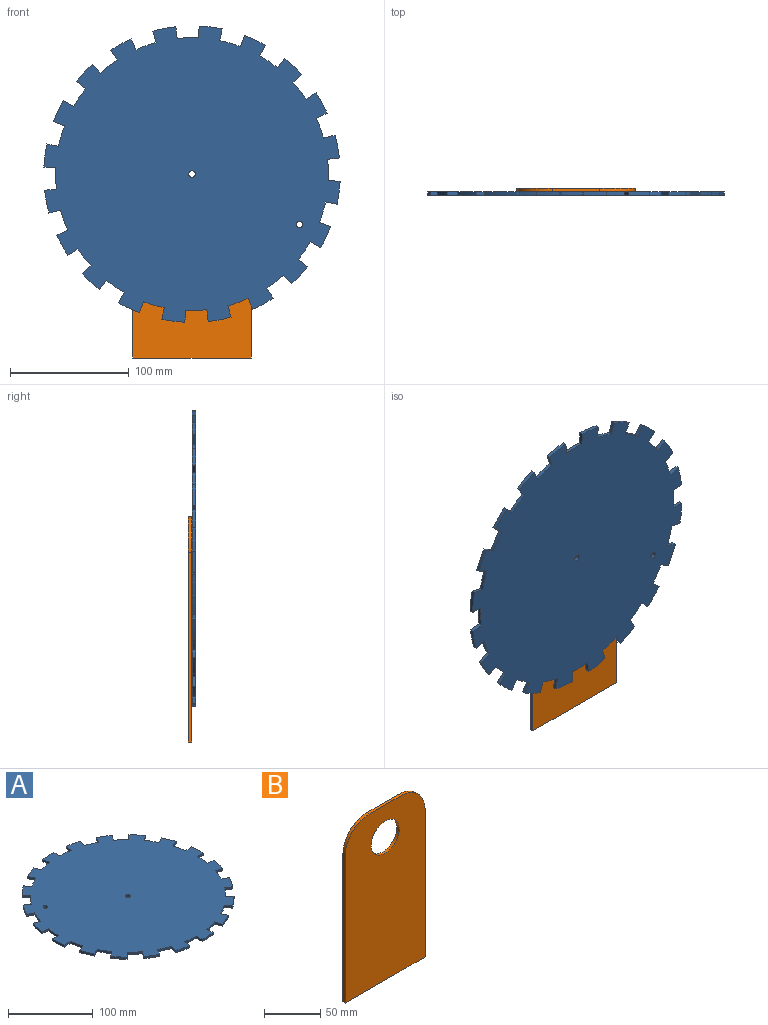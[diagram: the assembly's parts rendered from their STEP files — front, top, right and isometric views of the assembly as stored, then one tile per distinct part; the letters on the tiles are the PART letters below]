
ASSEMBLY  parts=2 mates=1
PART A: 84 faces, bbox 250x250x3 mm
  f0: plane 250x250mm, normal (0,0,1), area 45270mm2, adj f2,f3,f4,f5,f6,f7,f8,f9
  f1: plane 250x250mm, normal (0,0,-1), area 45270mm2, adj f2,f3,f4,f5,f6,f7,f8,f9
  f2: cylinder r=115mm len=17.98mm, axis (0,0,-1), area 54.2mm2, adj f0,f1,f3,f81
  f3: plane 10x3mm, normal (1,-0.01,0), area 30mm2, adj f0,f1,f2,f4
  f4: cylinder r=125mm len=19.57mm, axis (0,0,-1), area 58.9mm2, adj f0,f1,f3,f5
  f5: plane 9.89x3mm, normal (-0.99,-0.15,0), area 30mm2, adj f0,f1,f4,f6
  f6: cylinder r=115mm len=17.58mm, axis (0,0,-1), area 54.2mm2, adj f0,f1,f5,f7
  f7: plane 9.54x3.01mm, normal (0.95,0.3,0), area 30mm2, adj f0,f1,f6,f8
  f8: cylinder r=125mm len=18.18mm, axis (0,0,-1), area 58.9mm2, adj f0,f1,f7,f9
  f9: plane 8.95x4.46mm, normal (-0.89,-0.45,0), area 30mm2, adj f0,f1,f8,f10
  f10: cylinder r=115mm len=15.47mm, axis (0,0,-1), area 54.2mm2, adj f0,f1,f9,f11
  f11: plane 8.14x5.81mm, normal (0.81,0.58,0), area 30mm2, adj f0,f1,f10,f12
  f12: cylinder r=125mm len=15.02mm, axis (0,0,-1), area 58.9mm2, adj f0,f1,f11,f13
  f13: plane 7.13x7.01mm, normal (-0.71,-0.7,0), area 30mm2, adj f0,f1,f12,f14
  f14: cylinder r=115mm len=13.62mm, axis (0,0,-1), area 54.2mm2, adj f0,f1,f13,f15
  f15: plane 8.04x5.95mm, normal (0.59,0.8,0), area 30mm2, adj f0,f1,f14,f16
  f16: cylinder r=125mm len=16.64mm, axis (0,0,-1), area 58.9mm2, adj f0,f1,f15,f17
  f17: plane 8.87x4.62mm, normal (-0.46,-0.89,0), area 30mm2, adj f0,f1,f16,f18
  f18: cylinder r=115mm len=16.61mm, axis (0,0,-1), area 54.2mm2, adj f0,f1,f17,f19
  f19: plane 9.48x3.17mm, normal (0.32,0.95,0), area 30mm2, adj f0,f1,f18,f20
  f20: cylinder r=125mm len=19.03mm, axis (0,0,-1), area 58.9mm2, adj f0,f1,f19,f21
  f21: plane 9.86x3mm, normal (-0.16,-0.99,0), area 30mm2, adj f0,f1,f20,f22
  f22: cylinder r=115mm len=17.98mm, axis (0,0,-1), area 54.2mm2, adj f0,f1,f21,f23
  f23: plane 10x3mm, normal (0.01,1,0), area 30mm2, adj f0,f1,f22,f24
  f24: cylinder r=125mm len=19.57mm, axis (0,0,-1), area 58.9mm2, adj f0,f1,f23,f25
  f25: plane 9.89x3mm, normal (0.15,-0.99,0), area 30mm2, adj f0,f1,f24,f26
  f26: cylinder r=115mm len=17.58mm, axis (0,0,-1), area 54.2mm2, adj f0,f1,f25,f27
  f27: plane 9.54x3.01mm, normal (-0.3,0.95,0), area 30mm2, adj f0,f1,f26,f28
  f28: cylinder r=125mm len=18.18mm, axis (0,0,-1), area 58.9mm2, adj f0,f1,f27,f29
  f29: plane 8.95x4.46mm, normal (0.45,-0.89,0), area 30mm2, adj f0,f1,f28,f30
  f30: cylinder r=115mm len=15.47mm, axis (0,0,-1), area 54.2mm2, adj f0,f1,f29,f31
  f31: plane 8.14x5.81mm, normal (-0.58,0.81,0), area 30mm2, adj f0,f1,f30,f32
  f32: cylinder r=125mm len=15.02mm, axis (0,0,-1), area 58.9mm2, adj f0,f1,f31,f33
  f33: plane 7.13x7.01mm, normal (0.7,-0.71,0), area 30mm2, adj f0,f1,f32,f34
  f34: cylinder r=115mm len=13.62mm, axis (0,0,-1), area 54.2mm2, adj f0,f1,f33,f35
  f35: plane 8.04x5.95mm, normal (-0.8,0.59,0), area 30mm2, adj f0,f1,f34,f36
  f36: cylinder r=125mm len=16.64mm, axis (0,0,-1), area 58.9mm2, adj f0,f1,f35,f37
  f37: plane 8.87x4.62mm, normal (0.89,-0.46,0), area 30mm2, adj f0,f1,f36,f38
  f38: cylinder r=115mm len=16.61mm, axis (0,0,-1), area 54.2mm2, adj f0,f1,f37,f39
  f39: plane 9.48x3.17mm, normal (-0.95,0.32,0), area 30mm2, adj f0,f1,f38,f40
  f40: cylinder r=125mm len=19.03mm, axis (0,0,-1), area 58.9mm2, adj f0,f1,f39,f41
  f41: plane 9.86x3mm, normal (0.99,-0.16,0), area 30mm2, adj f0,f1,f40,f42
  f42: cylinder r=115mm len=17.98mm, axis (0,0,-1), area 54.2mm2, adj f0,f1,f41,f43
  f43: plane 10x3mm, normal (-1,0.01,0), area 30mm2, adj f0,f1,f42,f44
  f44: cylinder r=125mm len=19.57mm, axis (0,0,-1), area 58.9mm2, adj f0,f1,f43,f45
  f45: plane 9.89x3mm, normal (0.99,0.15,0), area 30mm2, adj f0,f1,f44,f46
  f46: cylinder r=115mm len=17.58mm, axis (0,0,-1), area 54.2mm2, adj f0,f1,f45,f47
  f47: plane 9.54x3.01mm, normal (-0.95,-0.3,0), area 30mm2, adj f0,f1,f46,f48
  f48: cylinder r=125mm len=18.18mm, axis (0,0,-1), area 58.9mm2, adj f0,f1,f47,f49
  f49: plane 8.95x4.46mm, normal (0.89,0.45,0), area 30mm2, adj f0,f1,f48,f50
  f50: cylinder r=115mm len=15.47mm, axis (0,0,-1), area 54.2mm2, adj f0,f1,f49,f51
  f51: plane 8.14x5.81mm, normal (-0.81,-0.58,0), area 30mm2, adj f0,f1,f50,f52
  f52: cylinder r=125mm len=15.02mm, axis (0,0,-1), area 58.9mm2, adj f0,f1,f51,f53
  f53: plane 7.13x7.01mm, normal (0.71,0.7,0), area 30mm2, adj f0,f1,f52,f54
  f54: cylinder r=115mm len=13.62mm, axis (0,0,-1), area 54.2mm2, adj f0,f1,f53,f55
  f55: plane 8.04x5.95mm, normal (-0.59,-0.8,0), area 30mm2, adj f0,f1,f54,f56
  f56: cylinder r=125mm len=16.64mm, axis (0,0,-1), area 58.9mm2, adj f0,f1,f55,f57
  f57: plane 8.87x4.62mm, normal (0.46,0.89,0), area 30mm2, adj f0,f1,f56,f58
  f58: cylinder r=115mm len=16.61mm, axis (0,0,-1), area 54.2mm2, adj f0,f1,f57,f59
  f59: plane 9.48x3.17mm, normal (-0.32,-0.95,0), area 30mm2, adj f0,f1,f58,f60
  f60: cylinder r=125mm len=19.03mm, axis (0,0,-1), area 58.9mm2, adj f0,f1,f59,f61
  f61: plane 9.86x3mm, normal (0.16,0.99,0), area 30mm2, adj f0,f1,f60,f62
  f62: cylinder r=115mm len=17.98mm, axis (0,0,-1), area 54.2mm2, adj f0,f1,f61,f63
  f63: plane 10x3mm, normal (-0.01,-1,0), area 30mm2, adj f0,f1,f62,f64
  f64: cylinder r=125mm len=19.57mm, axis (0,0,-1), area 58.9mm2, adj f0,f1,f63,f65
  f65: plane 9.89x3mm, normal (-0.15,0.99,0), area 30mm2, adj f0,f1,f64,f66
  f66: cylinder r=115mm len=17.58mm, axis (0,0,-1), area 54.2mm2, adj f0,f1,f65,f67
  f67: plane 9.54x3.01mm, normal (0.3,-0.95,0), area 30mm2, adj f0,f1,f66,f68
  f68: cylinder r=125mm len=18.18mm, axis (0,0,-1), area 58.9mm2, adj f0,f1,f67,f69
  f69: plane 8.95x4.46mm, normal (-0.45,0.89,0), area 30mm2, adj f0,f1,f68,f70
  f70: cylinder r=115mm len=15.47mm, axis (0,0,-1), area 54.2mm2, adj f0,f1,f69,f71
  f71: plane 8.14x5.81mm, normal (0.58,-0.81,0), area 30mm2, adj f0,f1,f70,f72
  f72: cylinder r=125mm len=15.02mm, axis (0,0,-1), area 58.9mm2, adj f0,f1,f71,f73
  f73: plane 7.13x7.01mm, normal (-0.7,0.71,0), area 30mm2, adj f0,f1,f72,f74
  f74: cylinder r=115mm len=13.62mm, axis (0,0,-1), area 54.2mm2, adj f0,f1,f73,f75
  f75: plane 8.04x5.95mm, normal (0.8,-0.59,0), area 30mm2, adj f0,f1,f74,f76
  f76: cylinder r=125mm len=16.64mm, axis (0,0,-1), area 58.9mm2, adj f0,f1,f75,f77
  f77: plane 8.87x4.62mm, normal (-0.89,0.46,0), area 30mm2, adj f0,f1,f76,f78
  f78: cylinder r=115mm len=16.61mm, axis (0,0,-1), area 54.2mm2, adj f0,f1,f77,f79
  f79: plane 9.48x3.17mm, normal (0.95,-0.32,0), area 30mm2, adj f0,f1,f78,f80
  f80: cylinder r=125mm len=19.03mm, axis (0,0,-1), area 58.9mm2, adj f0,f1,f79,f81
  f81: plane 9.86x3mm, normal (-0.99,0.16,0), area 30mm2, adj f0,f1,f2,f80
  f82: cylinder r=2.75mm len=5.5mm, axis (0,0,-1), area 51.8mm2, adj f0,f1
  f83: cylinder r=2.75mm len=5.5mm, axis (0,0,-1), area 51.8mm2, adj f0,f1
PART B: 9 faces, bbox 100x3x190 mm
  f0: plane 190x100mm, normal (0,-1,0), area 17651.6mm2, adj f2,f3,f4,f5,f6,f7,f8
  f1: plane 190x100mm, normal (0,1,0), area 17651.6mm2, adj f2,f3,f4,f5,f6,f7,f8
  f2: plane 160x3mm, normal (-1,0,0), area 480mm2, adj f0,f1,f3,f7
  f3: plane 100x3mm, normal (0,0,-1), area 300mm2, adj f0,f1,f2,f4
  f4: plane 160x3mm, normal (1,0,0), area 480mm2, adj f0,f1,f3,f5
  f5: cylinder r=30mm len=30mm, axis (0,1,0), area 141.4mm2, adj f0,f1,f4,f6
  f6: plane 40x3mm, normal (0,0,1), area 120mm2, adj f0,f1,f5,f7
  f7: cylinder r=30mm len=30mm, axis (0,1,0), area 141.4mm2, adj f0,f1,f2,f6
  f8: cylinder r=17.5mm len=35mm, axis (0,1,0), area 329.9mm2, adj f0,f1
PLACE A rot(axis=(-0.36,-0.66,-0.66),140.4deg) t=(-76.11,-42.53,68.86)mm
PLACE B t=(-126.11,-36.53,-86.14)mm fixed
MATE revolute B.f8 <-> A.f2  axis (0,-1,0) through (-76.11,-39.53,68.86)mm
